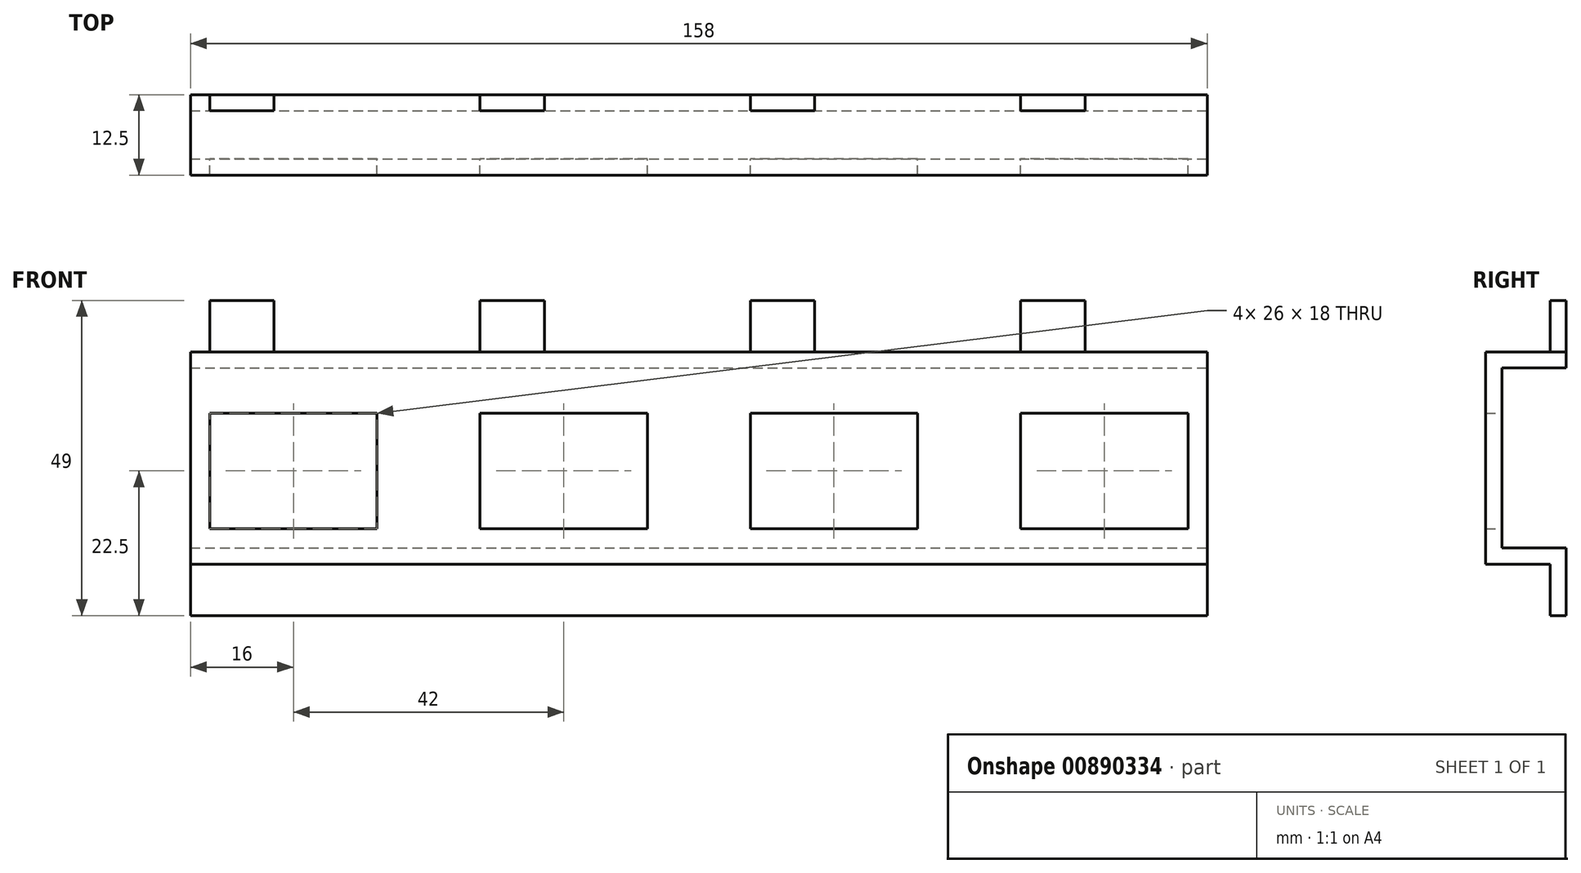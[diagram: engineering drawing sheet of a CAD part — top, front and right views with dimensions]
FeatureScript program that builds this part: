
annotation { "Feature Type Name" : "Feature", "Feature Type Description" : "" }
export const myFeature = defineFeature(function(context is Context, id is Id, definition is map)
    precondition{}
    {
        {
            var Q0;
            Q0=qCreatedBy(makeId("Right.planeOp"),FACE);
            var sketch = newSketch(context, id + "F0", { "sketchPlane" : qUnion([Q0])});
            skLineSegment(sketch, "E0", {"start": v(0, 0) * mm, "end": v(0, 10.5) * mm});
            skLineSegment(sketch, "E1", {"start": v(0, 10.5) * mm, "end": v(-10, 10.5) * mm});
            skLineSegment(sketch, "E2", {"start": v(-10, 10.5) * mm, "end": v(-10, 38.5) * mm});
            skLineSegment(sketch, "E3", {"start": v(-10, 38.5) * mm, "end": v(0, 38.5) * mm});
            skLineSegment(sketch, "E4", {"start": v(0, 38.5) * mm, "end": v(0, 49) * mm});
            skLineSegment(sketch, "E5.0", {"start": v(-2.5, 41) * mm, "end": v(-2.5, 49) * mm});
            skLineSegment(sketch, "E5.1", {"start": v(-2.5, 0) * mm, "end": v(-2.5, 8) * mm});
            skLineSegment(sketch, "E5.2", {"start": v(-2.5, 8) * mm, "end": v(-12.5, 8) * mm});
            skLineSegment(sketch, "E5.3", {"start": v(-12.5, 8) * mm, "end": v(-12.5, 41) * mm});
            skLineSegment(sketch, "E5.4", {"start": v(-12.5, 41) * mm, "end": v(-2.5, 41) * mm});
            skLineSegment(sketch, "E6", {"start": v(-2.5, 49) * mm, "end": v(0, 49) * mm});
            skLineSegment(sketch, "E7", {"start": v(-2.5, 0) * mm, "end": v(0, 0) * mm});
            skSolve(sketch);
        }
        {
            var Q0;
            Q0 = qSketchRegion(id + "F0", true);
            extrude(context, id + "F1", {"entities" : qUnion([Q0]), "depth" : 116 * mm, "offsetDistance" : 25 * mm});
        }
        {
            var Q0;
            Q0=qCreatedBy(makeId("Front.planeOp"),FACE);
            var sketch = newSketch(context, id + "F2", { "sketchPlane" : qUnion([Q0])});
            skLineSegment(sketch, "E8.bottom", {"start": v(3, 31.5) * mm, "end": v(29, 31.5) * mm});
            skLineSegment(sketch, "E8.top", {"start": v(3, 13.5) * mm, "end": v(29, 13.5) * mm});
            skLineSegment(sketch, "E8.left", {"start": v(3, 31.5) * mm, "end": v(3, 13.5) * mm});
            skLineSegment(sketch, "E8.right", {"start": v(29, 31.5) * mm, "end": v(29, 13.5) * mm});
            skLineSegment(sketch, "E9.bottom", {"start": v(45, 13.5) * mm, "end": v(71, 13.5) * mm});
            skLineSegment(sketch, "E9.top", {"start": v(45, 31.5) * mm, "end": v(71, 31.5) * mm});
            skLineSegment(sketch, "E9.left", {"start": v(45, 13.5) * mm, "end": v(45, 31.5) * mm});
            skLineSegment(sketch, "E9.right", {"start": v(71, 13.5) * mm, "end": v(71, 31.5) * mm});
            skLineSegment(sketch, "E10.bottom", {"start": v(87, 31.5) * mm, "end": v(113, 31.5) * mm});
            skLineSegment(sketch, "E10.top", {"start": v(87, 13.5) * mm, "end": v(113, 13.5) * mm});
            skLineSegment(sketch, "E10.left", {"start": v(87, 31.5) * mm, "end": v(87, 13.5) * mm});
            skLineSegment(sketch, "E10.right", {"start": v(113, 31.5) * mm, "end": v(113, 13.5) * mm});
            skSolve(sketch);
        }
        {
            var Q0;
            Q0 = qSketchRegion(id + "F2", true);
            extrude(context, id + "F3", {"entities" : qUnion([Q0]), "operationType" : NewBodyOperationType.REMOVE, "endBound" : BoundingType.THROUGH_ALL, "depth" : 25 * mm, "offsetDistance" : 25 * mm});
        }
        {
            var Q0;
            Q0=qCreatedBy(makeId("Front.planeOp"),FACE);
            var sketch = newSketch(context, id + "F4", { "sketchPlane" : qUnion([Q0])});
            skLineSegment(sketch, "E11.0", {"start": v(3, 31.5) * mm, "end": v(29, 31.5) * mm, "construction": true});
            skLineSegment(sketch, "E11.1", {"start": v(3, 13.5) * mm, "end": v(29, 13.5) * mm, "construction": true});
            skLineSegment(sketch, "E11.2", {"start": v(3, 31.5) * mm, "end": v(3, 13.5) * mm, "construction": true});
            skLineSegment(sketch, "E11.3", {"start": v(29, 31.5) * mm, "end": v(29, 13.5) * mm, "construction": true});
            skLineSegment(sketch, "E11.4", {"start": v(45, 13.5) * mm, "end": v(71, 13.5) * mm, "construction": true});
            skLineSegment(sketch, "E11.5", {"start": v(45, 31.5) * mm, "end": v(71, 31.5) * mm, "construction": true});
            skLineSegment(sketch, "E11.6", {"start": v(45, 13.5) * mm, "end": v(45, 31.5) * mm, "construction": true});
            skLineSegment(sketch, "E11.7", {"start": v(71, 13.5) * mm, "end": v(71, 31.5) * mm, "construction": true});
            skLineSegment(sketch, "E11.8", {"start": v(87, 31.5) * mm, "end": v(113, 31.5) * mm, "construction": true});
            skLineSegment(sketch, "E11.9", {"start": v(87, 13.5) * mm, "end": v(113, 13.5) * mm, "construction": true});
            skLineSegment(sketch, "E11.10", {"start": v(87, 31.5) * mm, "end": v(87, 13.5) * mm, "construction": true});
            skLineSegment(sketch, "E11.11", {"start": v(113, 31.5) * mm, "end": v(113, 13.5) * mm, "construction": true});
            skLineSegment(sketch, "E12.bottom", {"start": v(19, 8) * mm, "end": v(0, 8) * mm});
            skLineSegment(sketch, "E12.top", {"start": v(19, 0) * mm, "end": v(0, 0) * mm});
            skLineSegment(sketch, "E12.left", {"start": v(19, 8) * mm, "end": v(19, 0) * mm});
            skLineSegment(sketch, "E12.right", {"start": v(0, 8) * mm, "end": v(0, 0) * mm});
            skLineSegment(sketch, "E13.bottom", {"start": v(61, 8) * mm, "end": v(29, 8) * mm});
            skLineSegment(sketch, "E13.top", {"start": v(61, 0) * mm, "end": v(29, 0) * mm});
            skLineSegment(sketch, "E13.left", {"start": v(61, 8) * mm, "end": v(61, 0) * mm});
            skLineSegment(sketch, "E13.right", {"start": v(29, 8) * mm, "end": v(29, 0) * mm});
            skLineSegment(sketch, "E14.bottom", {"start": v(103, 8) * mm, "end": v(71, 8) * mm});
            skLineSegment(sketch, "E14.top", {"start": v(103, 0) * mm, "end": v(71, 0) * mm});
            skLineSegment(sketch, "E14.left", {"start": v(103, 8) * mm, "end": v(103, 0) * mm});
            skLineSegment(sketch, "E14.right", {"start": v(71, 8) * mm, "end": v(71, 0) * mm});
            skLineSegment(sketch, "E15.bottom", {"start": v(116, 0) * mm, "end": v(113, 0) * mm});
            skLineSegment(sketch, "E15.top", {"start": v(116, 8) * mm, "end": v(113, 8) * mm});
            skLineSegment(sketch, "E15.left", {"start": v(116, 0) * mm, "end": v(116, 8) * mm});
            skLineSegment(sketch, "E15.right", {"start": v(113, 0) * mm, "end": v(113, 8) * mm});
            skSolve(sketch);
        }
        {
            var Q0;
            Q0 = qSketchRegion(id + "F4", true);
            extrude(context, id + "F5", {"entities" : qUnion([Q0]), "operationType" : NewBodyOperationType.REMOVE, "endBound" : BoundingType.THROUGH_ALL, "depth" : 25 * mm, "offsetDistance" : 25 * mm});
        }
        {
            var Q0;
            Q0=makeQuery(id+"F1.opExtrude","SWEPT_BODY",BODY,{"disambiguationData":[OSD([sQuery(id+"F0.wireOp",EDGE,"E0"),sQuery(id+"F0.wireOp",EDGE,"E1"),sQuery(id+"F0.wireOp",EDGE,"E2"),sQuery(id+"F0.wireOp",EDGE,"E3"),sQuery(id+"F0.wireOp",EDGE,"E4"),sQuery(id+"F0.wireOp",EDGE,"E5.0"),sQuery(id+"F0.wireOp",EDGE,"E5.1"),sQuery(id+"F0.wireOp",EDGE,"E5.2"),sQuery(id+"F0.wireOp",EDGE,"E5.3"),sQuery(id+"F0.wireOp",EDGE,"E5.4"),sQuery(id+"F0.wireOp",EDGE,"E6"),sQuery(id+"F0.wireOp",EDGE,"E7")])]});
            deleteBodies(context, id + "F6", {"entities" : qUnion([Q0])});
        }
        {
            var Q0;
            Q0 = qSketchRegion(id + "F0", true);
            extrude(context, id + "F7", {"entities" : qUnion([Q0]), "oppositeDirection" : true, "depth" : 158 * mm, "offsetDistance" : 25 * mm});
        }
        {
            var Q0;
            Q0=qCreatedBy(makeId("Front.planeOp"),FACE);
            var sketch = newSketch(context, id + "F8", { "sketchPlane" : qUnion([Q0])});
            skLineSegment(sketch, "E16.bottom", {"start": v(-3, 31.5) * mm, "end": v(-29, 31.5) * mm});
            skLineSegment(sketch, "E16.top", {"start": v(-3, 13.5) * mm, "end": v(-29, 13.5) * mm});
            skLineSegment(sketch, "E16.left", {"start": v(-3, 31.5) * mm, "end": v(-3, 13.5) * mm});
            skLineSegment(sketch, "E16.right", {"start": v(-29, 31.5) * mm, "end": v(-29, 13.5) * mm});
            skLineSegment(sketch, "E17.bottom", {"start": v(-45, 31.5) * mm, "end": v(-71, 31.5) * mm});
            skLineSegment(sketch, "E17.top", {"start": v(-45, 13.5) * mm, "end": v(-71, 13.5) * mm});
            skLineSegment(sketch, "E17.left", {"start": v(-45, 31.5) * mm, "end": v(-45, 13.5) * mm});
            skLineSegment(sketch, "E17.right", {"start": v(-71, 31.5) * mm, "end": v(-71, 13.5) * mm});
            skLineSegment(sketch, "E18.bottom", {"start": v(-87, 31.5) * mm, "end": v(-113, 31.5) * mm});
            skLineSegment(sketch, "E18.top", {"start": v(-87, 13.5) * mm, "end": v(-113, 13.5) * mm});
            skLineSegment(sketch, "E18.left", {"start": v(-87, 31.5) * mm, "end": v(-87, 13.5) * mm});
            skLineSegment(sketch, "E18.right", {"start": v(-113, 31.5) * mm, "end": v(-113, 13.5) * mm});
            skLineSegment(sketch, "E19.bottom", {"start": v(-129, 31.5) * mm, "end": v(-155, 31.5) * mm});
            skLineSegment(sketch, "E19.top", {"start": v(-129, 13.5) * mm, "end": v(-155, 13.5) * mm});
            skLineSegment(sketch, "E19.left", {"start": v(-129, 31.5) * mm, "end": v(-129, 13.5) * mm});
            skLineSegment(sketch, "E19.right", {"start": v(-155, 31.5) * mm, "end": v(-155, 13.5) * mm});
            skSolve(sketch);
        }
        {
            var Q0;
            Q0 = qSketchRegion(id + "F8", true);
            extrude(context, id + "F9", {"entities" : qUnion([Q0]), "operationType" : NewBodyOperationType.REMOVE, "endBound" : BoundingType.THROUGH_ALL, "depth" : 25 * mm, "offsetDistance" : 25 * mm});
        }
        {
            var Q0;
            Q0=qCreatedBy(makeId("Front.planeOp"),FACE);
            var sketch = newSketch(context, id + "F10", { "sketchPlane" : qUnion([Q0])});
            skLineSegment(sketch, "E20.bottom", {"start": v(-19, 49) * mm, "end": v(0, 49) * mm});
            skLineSegment(sketch, "E20.top", {"start": v(-19, 41) * mm, "end": v(0, 41) * mm});
            skLineSegment(sketch, "E20.left", {"start": v(-19, 49) * mm, "end": v(-19, 41) * mm});
            skLineSegment(sketch, "E20.right", {"start": v(0, 49) * mm, "end": v(0, 41) * mm});
            skLineSegment(sketch, "E21.bottom", {"start": v(-29, 49) * mm, "end": v(-61, 49) * mm});
            skLineSegment(sketch, "E21.top", {"start": v(-29, 41) * mm, "end": v(-61, 41) * mm});
            skLineSegment(sketch, "E21.left", {"start": v(-29, 49) * mm, "end": v(-29, 41) * mm});
            skLineSegment(sketch, "E21.right", {"start": v(-61, 49) * mm, "end": v(-61, 41) * mm});
            skLineSegment(sketch, "E22.bottom", {"start": v(-71, 49) * mm, "end": v(-103, 49) * mm});
            skLineSegment(sketch, "E22.top", {"start": v(-71, 41) * mm, "end": v(-103, 41) * mm});
            skLineSegment(sketch, "E22.left", {"start": v(-71, 49) * mm, "end": v(-71, 41) * mm});
            skLineSegment(sketch, "E22.right", {"start": v(-103, 49) * mm, "end": v(-103, 41) * mm});
            skLineSegment(sketch, "E23.bottom", {"start": v(-113, 41) * mm, "end": v(-145, 41) * mm});
            skLineSegment(sketch, "E23.top", {"start": v(-113, 49) * mm, "end": v(-145, 49) * mm});
            skLineSegment(sketch, "E23.left", {"start": v(-113, 41) * mm, "end": v(-113, 49) * mm});
            skLineSegment(sketch, "E23.right", {"start": v(-145, 41) * mm, "end": v(-145, 49) * mm});
            skLineSegment(sketch, "E24.bottom", {"start": v(-158, 41) * mm, "end": v(-155, 41) * mm});
            skLineSegment(sketch, "E24.top", {"start": v(-158, 49) * mm, "end": v(-155, 49) * mm});
            skLineSegment(sketch, "E24.left", {"start": v(-158, 41) * mm, "end": v(-158, 49) * mm});
            skLineSegment(sketch, "E24.right", {"start": v(-155, 41) * mm, "end": v(-155, 49) * mm});
            skSolve(sketch);
        }
        {
            var Q0;
            Q0 = qSketchRegion(id + "F10", true);
            extrude(context, id + "F11", {"entities" : qUnion([Q0]), "operationType" : NewBodyOperationType.REMOVE, "endBound" : BoundingType.THROUGH_ALL, "depth" : 25 * mm, "offsetDistance" : 25 * mm});
        }
    });
